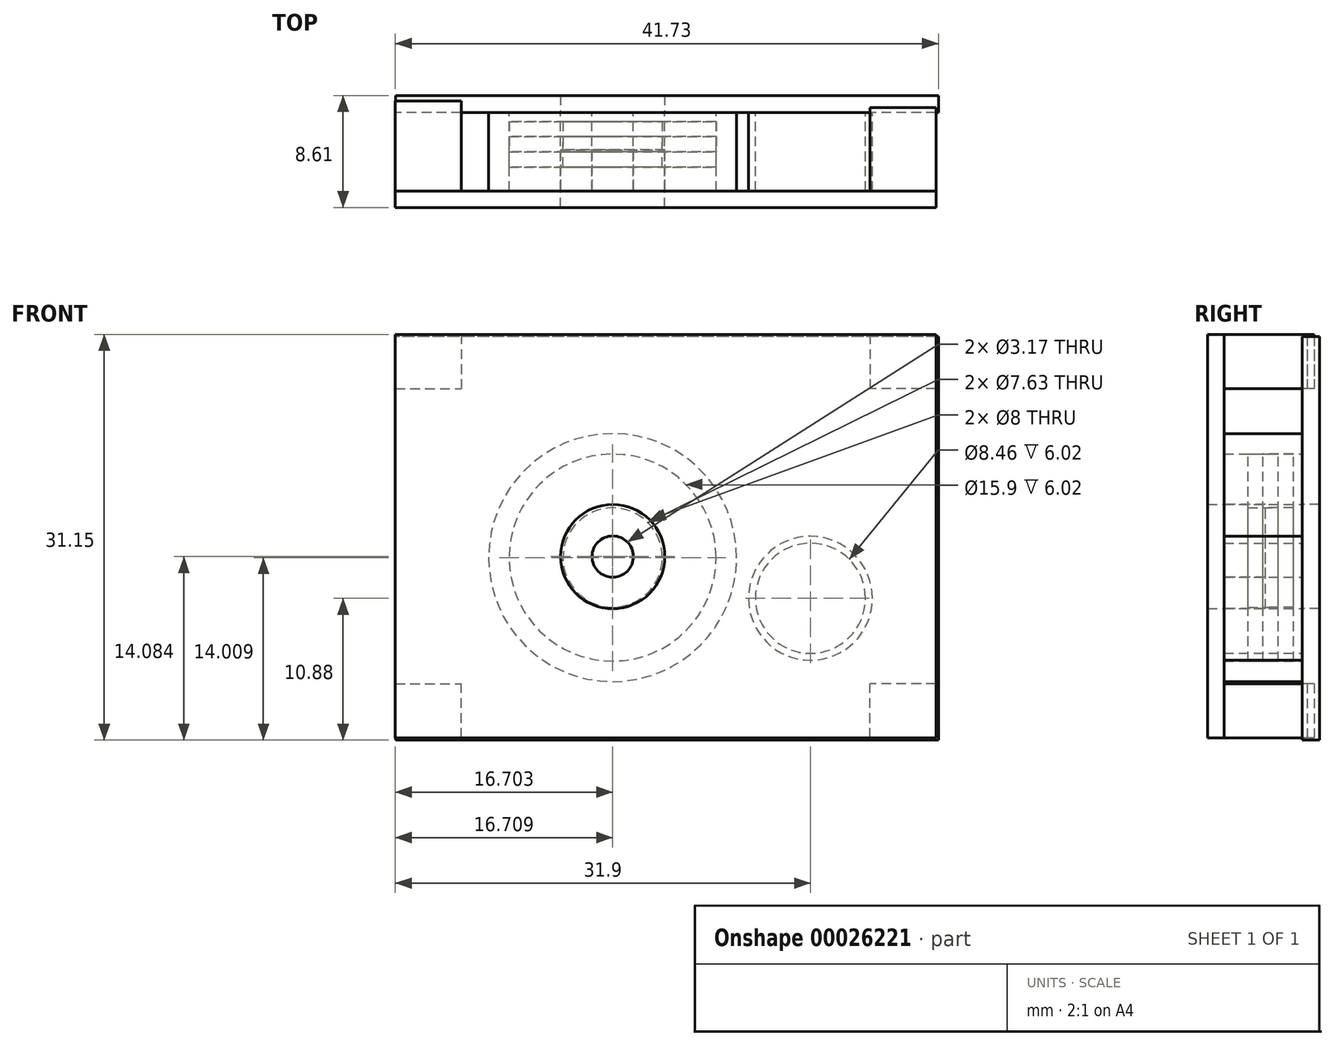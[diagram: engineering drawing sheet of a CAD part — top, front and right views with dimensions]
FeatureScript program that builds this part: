
annotation { "Feature Type Name" : "Feature", "Feature Type Description" : "" }
export const myFeature = defineFeature(function(context is Context, id is Id, definition is map)
    precondition{}
    {
        {
            var Q0;
            Q0=qCreatedBy(makeId("Front.planeOp"),FACE);
            var sketch = newSketch(context, id + "F0", { "sketchPlane" : qUnion([Q0])});
            skCircle(sketch, "E0", {"center": v(0, 0) * mm, "radius": 4.76 * mm});
            skCircle(sketch, "E1", {"center": v(0, 0) * mm, "radius": 1.59 * mm});
            skCircle(sketch, "E2", {"center": v(0, 0) * mm, "radius": 4.23 * mm});
            skCircle(sketch, "E3", {"center": v(-15.2, 3.13) * mm, "radius": 9.53 * mm});
            skCircle(sketch, "E4", {"center": v(-15.2, 3.13) * mm, "radius": 1.59 * mm});
            skCircle(sketch, "E5", {"center": v(-15.2, 3.13) * mm, "radius": 7.95 * mm});
            skCircle(sketch, "E6", {"center": v(-15.2, 3.13) * mm, "radius": 3.82 * mm});
            skLineSegment(sketch, "E7.bottom", {"start": v(-32.78, 19.52) * mm, "end": v(8.94, 19.52) * mm});
            skLineSegment(sketch, "E7.top", {"start": v(-32.78, -11.47) * mm, "end": v(8.94, -11.47) * mm});
            skLineSegment(sketch, "E7.left", {"start": v(-32.78, 19.52) * mm, "end": v(-32.78, -11.47) * mm});
            skLineSegment(sketch, "E7.right", {"start": v(8.94, 19.52) * mm, "end": v(8.94, -11.47) * mm});
            skSolve(sketch);
        }
        {
            var Q0;
            Q0=makeQuery(id+"F0.imprint","IMPRINT",FACE,{"disambiguationData":[TD([[makeQuery(id+"F0.imprint","IMPRINT",EDGE,{"derivedFrom":sQuery(id+"F0.wireOp",EDGE,"E0")}),1.0]])]});
            var Q1;
            Q1=makeQuery(id+"F0.imprint","IMPRINT",FACE,{"disambiguationData":[TD([[makeQuery(id+"F0.imprint","IMPRINT",EDGE,{"derivedFrom":sQuery(id+"F0.wireOp",EDGE,"E3")}),1.0]])]});
            extrude(context, id + "F1", {"entities" : qUnion([Q0, Q1]), "endBound" : BoundingType.SYMMETRIC, "depth" : 6.02 * mm});
        }
        {
            var Q0;
            Q0=makeQuery(id+"F0.imprint","IMPRINT",FACE,{"disambiguationData":[TD([[makeQuery(id+"F0.imprint","IMPRINT",EDGE,{"derivedFrom":sQuery(id+"F0.wireOp",EDGE,"E5")}),1.0]])]});
            extrude(context, id + "F2", {"entities" : qUnion([Q0]), "endBound" : BoundingType.SYMMETRIC, "depth" : 2.34 * mm});
        }
        {
            var Q0;
            Q0=makeQuery(id+"F2.opExtrude","CAP_FACE",FACE,{"disambiguationData":[OSD([sQuery(id+"F0.wireOp",EDGE,"E5"),sQuery(id+"F0.wireOp",EDGE,"E6")])],"isStart":true});
            extrude(context, id + "F3", {"entities" : qUnion([Q0]), "endBound" : BoundingType.SYMMETRIC, "depth" : 2.34 * mm});
        }
        {
            var Q0;
            Q0=qCreatedBy(makeId("Front.planeOp"),FACE);
            var sketch = newSketch(context, id + "F4", { "sketchPlane" : qUnion([Q0])});
            skCircle(sketch, "E8", {"center": v(-15.2, 3.2) * mm, "radius": 4 * mm});
            skCircle(sketch, "E9", {"center": v(-15.2, 3.2) * mm, "radius": 1.59 * mm});
            skSolve(sketch);
        }
        {
            var Q0;
            Q0 = qSketchRegion(id + "F4", true);
            extrude(context, id + "F5", {"entities" : qUnion([Q0]), "endBound" : BoundingType.SYMMETRIC, "depth" : 6.02 * mm});
        }
        {
            var Q0;
            Q0=makeQuery(id+"F5.opExtrude","CAP_FACE",FACE,{"disambiguationData":[OSD([sQuery(id+"F4.wireOp",EDGE,"E8"),sQuery(id+"F4.wireOp",EDGE,"E9")])],"isStart":false});
            var sketch = newSketch(context, id + "F6", { "sketchPlane" : qUnion([Q0])});
            skLineSegment(sketch, "E10.bottom", {"start": v(-31.9, 20.27) * mm, "end": v(9.65, 20.27) * mm});
            skLineSegment(sketch, "E10.top", {"start": v(-31.9, -10.72) * mm, "end": v(9.65, -10.72) * mm});
            skLineSegment(sketch, "E10.left", {"start": v(-31.9, 20.27) * mm, "end": v(-31.9, -10.72) * mm});
            skLineSegment(sketch, "E10.right", {"start": v(9.65, 20.27) * mm, "end": v(9.65, -10.72) * mm});
            skSolve(sketch);
        }
        {
            var Q0;
            Q0=makeQuery(id+"F6.imprint","IMPRINT",FACE,{"disambiguationData":[TD([[makeQuery(id+"F6.imprint","IMPRINT",EDGE,{"derivedFrom":sQuery(id+"F6.wireOp",EDGE,"E10.bottom")}),-1.0]])]});
            extrude(context, id + "F7", {"entities" : qUnion([Q0]), "depth" : 1.26 * mm});
        }
        {
            var Q0;
            Q0=makeQuery(id+"F5.opExtrude","CAP_FACE",FACE,{"disambiguationData":[OSD([sQuery(id+"F4.wireOp",EDGE,"E8"),sQuery(id+"F4.wireOp",EDGE,"E9")])],"isStart":true});
            var sketch = newSketch(context, id + "F8", { "sketchPlane" : qUnion([Q0])});
            skLineSegment(sketch, "E11.bottom", {"start": v(-9.83, 20.11) * mm, "end": v(31.88, 20.11) * mm});
            skLineSegment(sketch, "E11.top", {"start": v(-9.83, -10.88) * mm, "end": v(31.88, -10.88) * mm});
            skLineSegment(sketch, "E11.left", {"start": v(-9.83, 20.11) * mm, "end": v(-9.83, -10.88) * mm});
            skLineSegment(sketch, "E11.right", {"start": v(31.88, 20.11) * mm, "end": v(31.88, -10.88) * mm});
            skSolve(sketch);
        }
        {
            var Q0;
            Q0=makeQuery(id+"F8.imprint","IMPRINT",FACE,{"disambiguationData":[TD([[makeQuery(id+"F8.imprint","IMPRINT",EDGE,{"derivedFrom":sQuery(id+"F8.wireOp",EDGE,"E11.bottom")}),-1.0]])]});
            extrude(context, id + "F9", {"entities" : qUnion([Q0]), "depth" : 1.33 * mm});
        }
        {
            var Q0;
            Q0=makeQuery(id+"F7.opExtrude","CAP_FACE",FACE,{"disambiguationData":[OSD([sQuery(id+"F4.wireOp",EDGE,"E8"),sQuery(id+"F6.wireOp",EDGE,"E10.bottom"),sQuery(id+"F6.wireOp",EDGE,"E10.top"),sQuery(id+"F6.wireOp",EDGE,"E10.left"),sQuery(id+"F6.wireOp",EDGE,"E10.right")])],"isStart":true});
            var sketch = newSketch(context, id + "F10", { "sketchPlane" : qUnion([Q0])});
            skLineSegment(sketch, "E12.bottom", {"start": v(31.9, 20.27) * mm, "end": v(26.82, 20.27) * mm});
            skLineSegment(sketch, "E12.top", {"start": v(31.9, 16.1) * mm, "end": v(26.82, 16.1) * mm});
            skLineSegment(sketch, "E12.left", {"start": v(31.9, 20.27) * mm, "end": v(31.9, 16.1) * mm});
            skLineSegment(sketch, "E12.right", {"start": v(26.82, 20.27) * mm, "end": v(26.82, 16.1) * mm});
            skLineSegment(sketch, "E13.bottom", {"start": v(31.9, -10.72) * mm, "end": v(26.82, -10.72) * mm});
            skLineSegment(sketch, "E13.top", {"start": v(31.9, -6.55) * mm, "end": v(26.82, -6.55) * mm});
            skLineSegment(sketch, "E13.left", {"start": v(31.9, -10.72) * mm, "end": v(31.9, -6.55) * mm});
            skLineSegment(sketch, "E13.right", {"start": v(26.82, -10.72) * mm, "end": v(26.82, -6.55) * mm});
            skLineSegment(sketch, "E14.bottom", {"start": v(-9.65, 20.27) * mm, "end": v(-4.57, 20.27) * mm});
            skLineSegment(sketch, "E14.top", {"start": v(-9.65, 16.1) * mm, "end": v(-4.57, 16.1) * mm});
            skLineSegment(sketch, "E14.left", {"start": v(-9.65, 20.27) * mm, "end": v(-9.65, 16.1) * mm});
            skLineSegment(sketch, "E14.right", {"start": v(-4.57, 20.27) * mm, "end": v(-4.57, 16.1) * mm});
            skLineSegment(sketch, "E15.bottom", {"start": v(-9.65, -10.72) * mm, "end": v(-4.57, -10.72) * mm});
            skLineSegment(sketch, "E15.top", {"start": v(-9.65, -6.55) * mm, "end": v(-4.57, -6.55) * mm});
            skLineSegment(sketch, "E15.left", {"start": v(-9.65, -10.72) * mm, "end": v(-9.65, -6.55) * mm});
            skLineSegment(sketch, "E15.right", {"start": v(-4.57, -10.72) * mm, "end": v(-4.57, -6.55) * mm});
            skSolve(sketch);
        }
        {
            var Q0;
            Q0=makeQuery(id+"F10.imprint","IMPRINT",FACE,{"disambiguationData":[TD([[makeQuery(id+"F10.imprint","IMPRINT",EDGE,{"derivedFrom":sQuery(id+"F10.wireOp",EDGE,"E12.bottom")}),1.0]])]});
            var Q1;
            Q1=makeQuery(id+"F10.imprint","IMPRINT",FACE,{"disambiguationData":[TD([[makeQuery(id+"F10.imprint","IMPRINT",EDGE,{"derivedFrom":sQuery(id+"F10.wireOp",EDGE,"E13.bottom")}),-1.0]])]});
            extrude(context, id + "F11", {"entities" : qUnion([Q0, Q1]), "depth" : 6.93 * mm});
        }
        {
            var Q0;
            Q0=makeQuery(id+"F10.imprint","IMPRINT",FACE,{"disambiguationData":[TD([[makeQuery(id+"F10.imprint","IMPRINT",EDGE,{"derivedFrom":sQuery(id+"F10.wireOp",EDGE,"E14.bottom")}),1.0]])]});
            var Q1;
            Q1=makeQuery(id+"F10.imprint","IMPRINT",FACE,{"disambiguationData":[TD([[makeQuery(id+"F10.imprint","IMPRINT",EDGE,{"derivedFrom":sQuery(id+"F10.wireOp",EDGE,"E15.bottom")}),-1.0]])]});
            extrude(context, id + "F12", {"entities" : qUnion([Q0, Q1]), "depth" : 6.4 * mm});
        }
        {
            var Q0;
            Q0=makeQuery(id+"F5.opExtrude","CAP_FACE",FACE,{"disambiguationData":[OSD([sQuery(id+"F4.wireOp",EDGE,"E8"),sQuery(id+"F4.wireOp",EDGE,"E9")])],"isStart":false});
            extrude(context, id + "F13", {"entities" : qUnion([Q0]), "oppositeDirection" : true, "depth" : 3.17 * mm});
        }
    });
